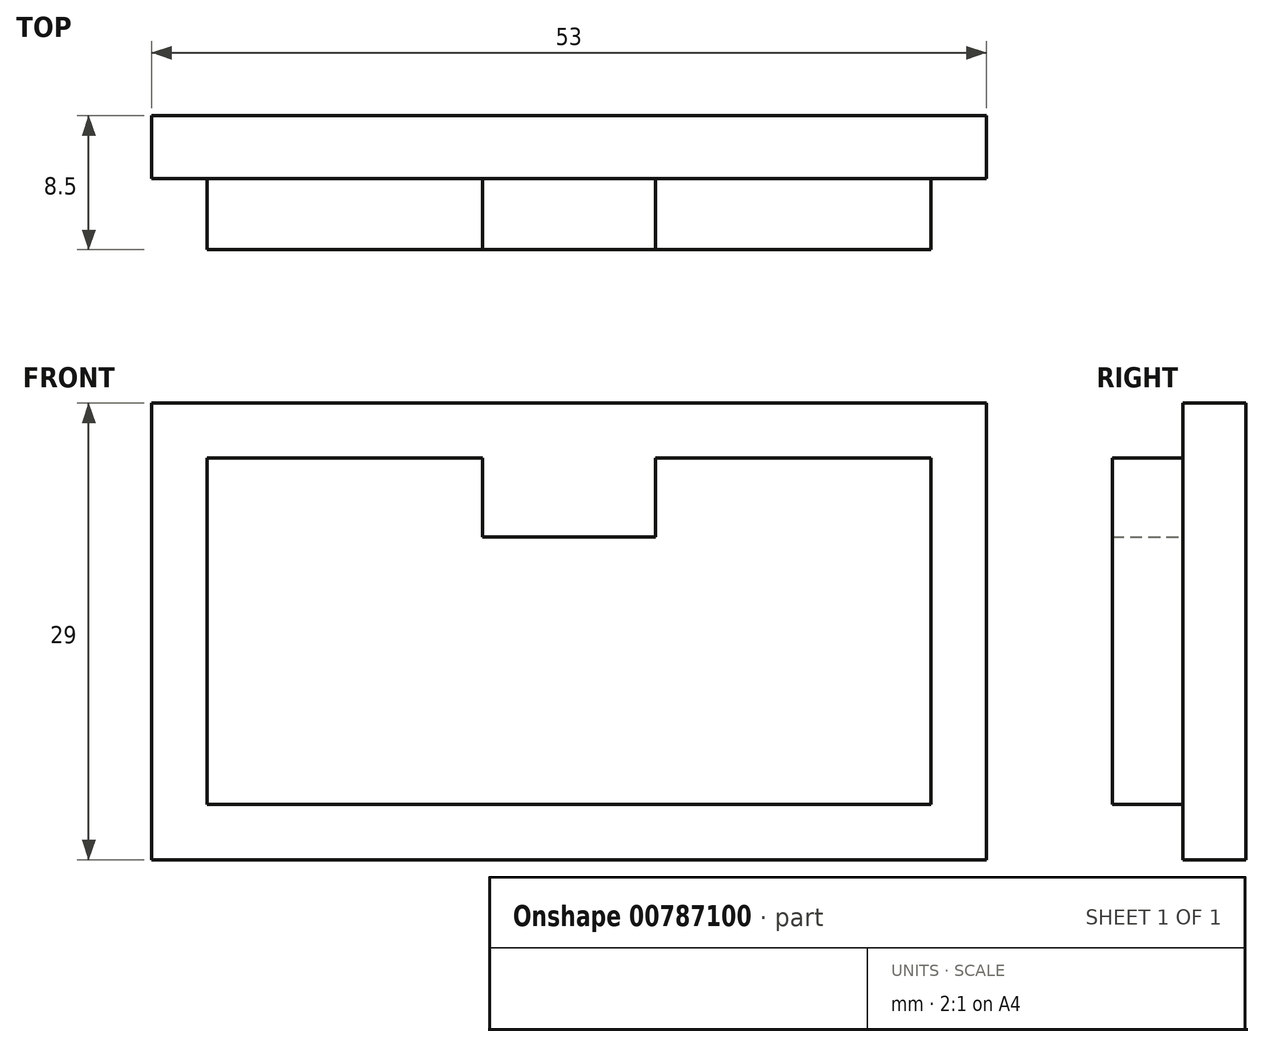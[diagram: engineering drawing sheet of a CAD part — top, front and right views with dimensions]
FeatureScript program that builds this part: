
annotation { "Feature Type Name" : "Feature", "Feature Type Description" : "" }
export const myFeature = defineFeature(function(context is Context, id is Id, definition is map)
    precondition{}
    {
        {
            var Q0;
            Q0=qCreatedBy(makeId("Front.planeOp"),FACE);
            var sketch = newSketch(context, id + "F0", { "sketchPlane" : qUnion([Q0])});
            skLineSegment(sketch, "E0.bottom", {"start": v(-26.5, 14.5) * mm, "end": v(26.5, 14.5) * mm});
            skLineSegment(sketch, "E0.top", {"start": v(-26.5, -14.5) * mm, "end": v(26.5, -14.5) * mm});
            skLineSegment(sketch, "E0.left", {"start": v(-26.5, 14.5) * mm, "end": v(-26.5, -14.5) * mm});
            skLineSegment(sketch, "E0.right", {"start": v(26.5, 14.5) * mm, "end": v(26.5, -14.5) * mm});
            skPoint(sketch, "E0.middle", {"position": v(0, 0) * mm});
            skLineSegment(sketch, "E1.bottom", {"start": v(-23, 11) * mm, "end": v(23, 11) * mm});
            skLineSegment(sketch, "E1.top", {"start": v(-23, -11) * mm, "end": v(23, -11) * mm});
            skLineSegment(sketch, "E1.left", {"start": v(-23, 11) * mm, "end": v(-23, -11) * mm});
            skLineSegment(sketch, "E1.right", {"start": v(23, 11) * mm, "end": v(23, -11) * mm});
            skPoint(sketch, "E2", {"position": v(0, 14.5) * mm});
            skPoint(sketch, "E3", {"position": v(0, 11) * mm});
            skLineSegment(sketch, "E4", {"start": v(0, 14.5) * mm, "end": v(0, 11) * mm});
            skPoint(sketch, "E5", {"position": v(0, 12.75) * mm});
            skLineSegment(sketch, "E6.bottom", {"start": v(-5.5, 14.5) * mm, "end": v(5.5, 14.5) * mm});
            skLineSegment(sketch, "E6.top", {"start": v(-5.5, 11) * mm, "end": v(5.5, 11) * mm});
            skLineSegment(sketch, "E6.left", {"start": v(-5.5, 14.5) * mm, "end": v(-5.5, 11) * mm});
            skLineSegment(sketch, "E6.right", {"start": v(5.5, 14.5) * mm, "end": v(5.5, 11) * mm});
            skLineSegment(sketch, "E7.left", {"start": v(-5.5, 11) * mm, "end": v(-5.5, 11) * mm});
            skLineSegment(sketch, "E7.right", {"start": v(5.5, 11) * mm, "end": v(5.5, 11) * mm});
            skLineSegment(sketch, "E8.top", {"start": v(-5.5, 6) * mm, "end": v(5.5, 6) * mm});
            skLineSegment(sketch, "E8.left", {"start": v(-5.5, 11) * mm, "end": v(-5.5, 6) * mm});
            skLineSegment(sketch, "E8.right", {"start": v(5.5, 11) * mm, "end": v(5.5, 6) * mm});
            skSolve(sketch);
        }
        {
            var Q0;
            Q0=makeQuery(id+"F0.imprint","IMPRINT",FACE,{"disambiguationData":[TD([[makeQuery(id+"F0.imprint","IMPRINT",EDGE,{"derivedFrom":sQuery(id+"F0.wireOp",EDGE,"E0.top")}),1.0]])]});
            var Q1;
            {var subQ0=sQuery(id+"F0.wireOp",EDGE,"E4");Q1=makeQuery(id+"F0.imprint","IMPRINT",FACE,{"disambiguationData":[TD([[makeQuery(id+"F0.imprint","IMPRINT",EDGE,{"derivedFrom":subQ0}),-1.0]])]});}
            var Q2;
            {var subQ2=sQuery(id+"F0.wireOp",EDGE,"E4");Q2=makeQuery(id+"F0.imprint","IMPRINT",FACE,{"disambiguationData":[TD([[makeQuery(id+"F0.imprint","IMPRINT",EDGE,{"derivedFrom":subQ2}),1.0]])]});}
            var Q3;
            Q3=makeQuery(id+"F0.imprint","IMPRINT",FACE,{"disambiguationData":[TD([[makeQuery(id+"F0.imprint","IMPRINT",EDGE,{"derivedFrom":sQuery(id+"F0.wireOp",EDGE,"E8.top")}),1.0]])]});
            extrude(context, id + "F1", {"entities" : qUnion([Q0, Q1, Q2, Q3]), "depth" : 4 * mm, "offsetDistance" : 25 * mm});
        }
        {
            var Q0;
            Q0=makeQuery(id+"F0.imprint","IMPRINT",FACE,{"disambiguationData":[TD([[makeQuery(id+"F0.imprint","IMPRINT",EDGE,{"derivedFrom":sQuery(id+"F0.wireOp",EDGE,"E1.top")}),1.0]])]});
            extrude(context, id + "F2", {"entities" : qUnion([Q0]), "operationType" : NewBodyOperationType.ADD, "depth" : 8.5 * mm, "offsetDistance" : 25 * mm});
        }
        {
            var Q0;
            {var subQ0=sQuery(id+"F0.wireOp",EDGE,"E4");Q0=makeQuery(id+"F0.imprint","IMPRINT",FACE,{"disambiguationData":[TD([[makeQuery(id+"F0.imprint","IMPRINT",EDGE,{"derivedFrom":subQ0}),-1.0]])]});}
            var Q1;
            {var subQ2=sQuery(id+"F0.wireOp",EDGE,"E4");Q1=makeQuery(id+"F0.imprint","IMPRINT",FACE,{"disambiguationData":[TD([[makeQuery(id+"F0.imprint","IMPRINT",EDGE,{"derivedFrom":subQ2}),1.0]])]});}
            var Q2;
            Q2=makeQuery(id+"F0.imprint","IMPRINT",FACE,{"disambiguationData":[TD([[makeQuery(id+"F0.imprint","IMPRINT",EDGE,{"derivedFrom":sQuery(id+"F0.wireOp",EDGE,"E8.top")}),1.0]])]});
            extrude(context, id + "F3", {"entities" : qUnion([Q0, Q1, Q2]), "operationType" : NewBodyOperationType.ADD, "depth" : 1 * mm, "offsetDistance" : 25 * mm});
        }
    });
